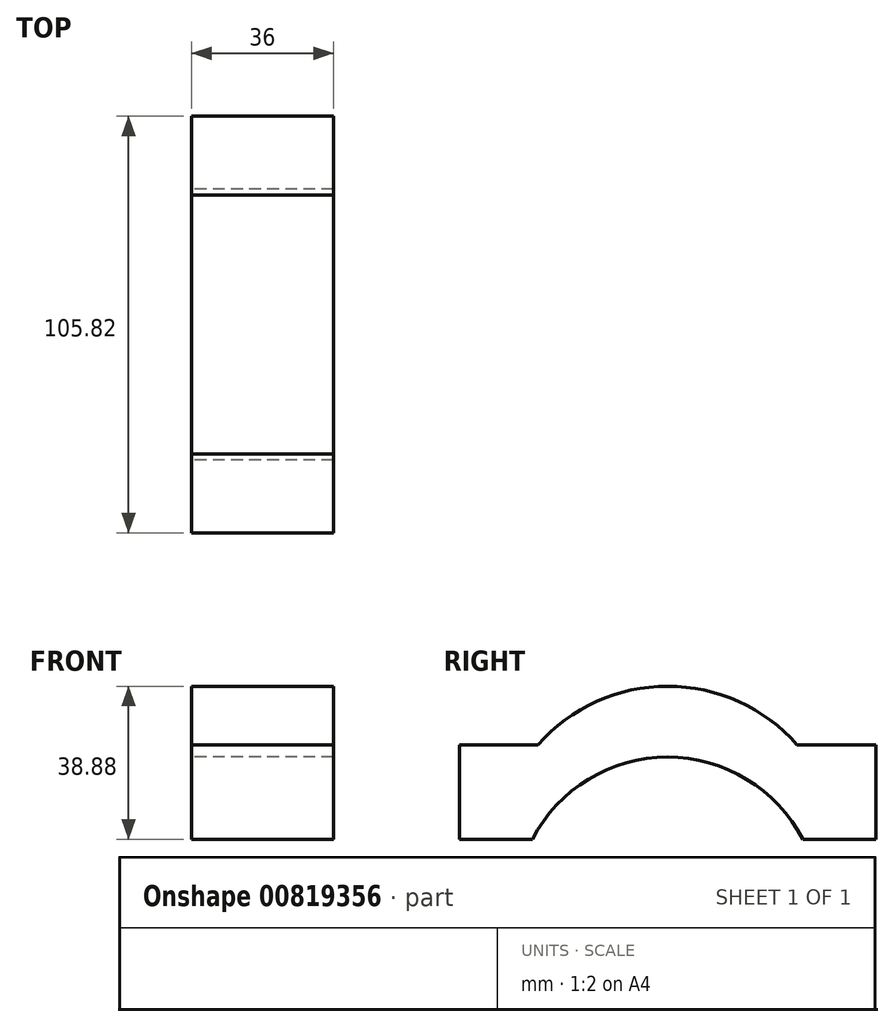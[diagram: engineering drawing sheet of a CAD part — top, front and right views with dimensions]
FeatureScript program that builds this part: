
annotation { "Feature Type Name" : "Feature", "Feature Type Description" : "" }
export const myFeature = defineFeature(function(context is Context, id is Id, definition is map)
    precondition{}
    {
        {
            var Q0;
            Q0=qCreatedBy(makeId("Right.planeOp"),FACE);
            var sketch = newSketch(context, id + "F0", { "sketchPlane" : qUnion([Q0])});
            skLineSegment(sketch, "E0", {"start": v(52.9, 0) * mm, "end": v(34.36, 0) * mm});
            skLineSegment(sketch, "E1.MirrorCS", {"start": v(-52.9, 0) * mm, "end": v(-34.36, 0) * mm});
            skArc(sketch, "E2", {"start": v(34.36, 0) * mm, "mid": v(0, 20.88) * mm, "end": v(-34.36, 0) * mm});
            skLineSegment(sketch, "E3", {"start": v(-52.9, 0) * mm, "end": v(-52.9, 24) * mm});
            skLineSegment(sketch, "E4", {"start": v(-52.9, 24) * mm, "end": v(-32.9, 24) * mm});
            skLineSegment(sketch, "E5.MirrorCS", {"start": v(52.9, 24) * mm, "end": v(32.9, 24) * mm});
            skLineSegment(sketch, "E6.MirrorCS", {"start": v(52.9, 0) * mm, "end": v(52.9, 24) * mm});
            skArc(sketch, "E7", {"start": v(32.9, 24) * mm, "mid": v(0, 38.88) * mm, "end": v(-32.9, 24) * mm});
            skSolve(sketch);
        }
        {
            var Q0;
            Q0=makeQuery(id+"F0.imprint","IMPRINT",FACE,{"disambiguationData":[TD([[makeQuery(id+"F0.imprint","IMPRINT",EDGE,{"derivedFrom":sQuery(id+"F0.wireOp",EDGE,"E0")}),-1.0]])]});
            extrude(context, id + "F1", {"entities" : qUnion([Q0]), "depth" : 36 * mm, "offsetDistance" : 25 * mm});
        }
    });
